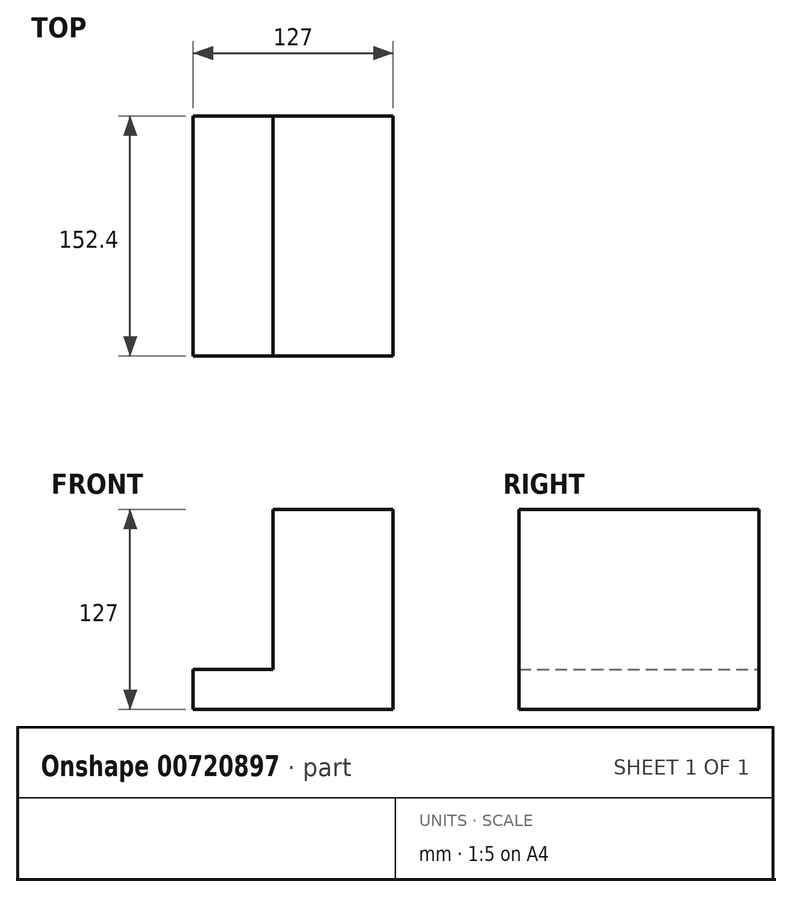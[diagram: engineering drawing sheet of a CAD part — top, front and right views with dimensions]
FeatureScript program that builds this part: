
annotation { "Feature Type Name" : "Feature", "Feature Type Description" : "" }
export const myFeature = defineFeature(function(context is Context, id is Id, definition is map)
    precondition{}
    {
        {
            var Q0;
            Q0=qCreatedBy(makeId("Front.planeOp"),FACE);
            var sketch = newSketch(context, id + "F0", { "sketchPlane" : qUnion([Q0])});
            skLineSegment(sketch, "E0", {"start": v(-50.08, -60) * mm, "end": v(76.92, -60) * mm});
            skLineSegment(sketch, "E1", {"start": v(-50.08, -60) * mm, "end": v(-50.08, -34.6) * mm});
            skLineSegment(sketch, "E2", {"start": v(-50.08, -34.6) * mm, "end": v(0.72, -34.6) * mm});
            skLineSegment(sketch, "E3", {"start": v(0.72, -34.6) * mm, "end": v(0.72, 67) * mm});
            skLineSegment(sketch, "E4", {"start": v(76.92, -60) * mm, "end": v(76.92, 67) * mm});
            skLineSegment(sketch, "E5", {"start": v(0.72, 67) * mm, "end": v(76.92, 67) * mm});
            skSolve(sketch);
        }
        {
            var Q0;
            Q0=makeQuery(id+"F0.imprint","IMPRINT",FACE,{"disambiguationData":[TD([[makeQuery(id+"F0.imprint","IMPRINT",EDGE,{"derivedFrom":sQuery(id+"F0.wireOp",EDGE,"E0")}),1.0]])]});
            extrude(context, id + "F1", {"entities" : qUnion([Q0]), "depth" : 152.4 * mm, "offsetDistance" : 25.4 * mm});
        }
    });
